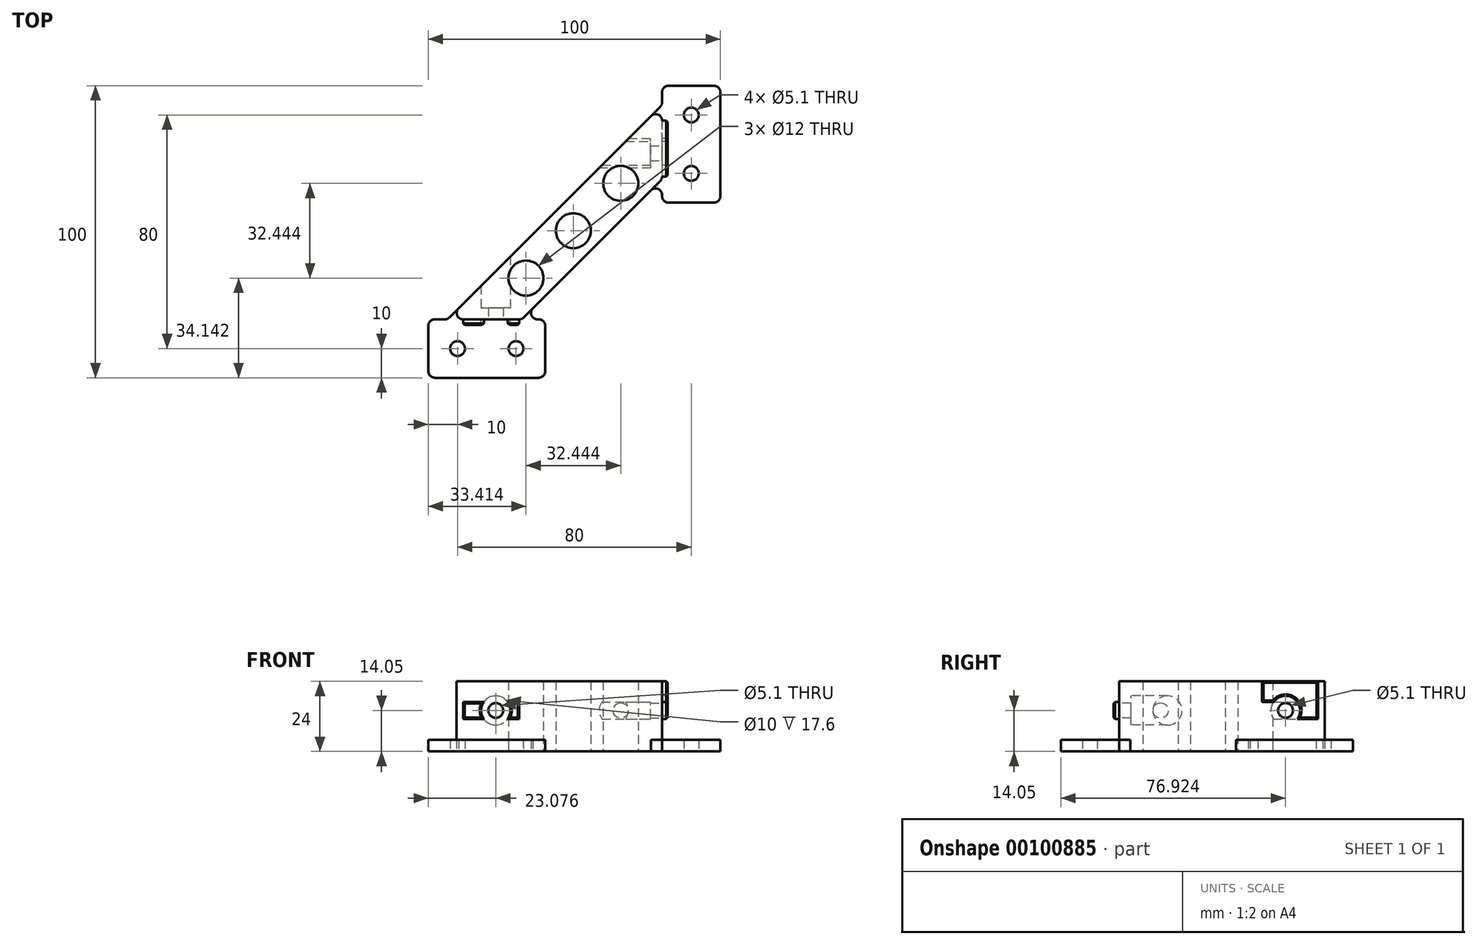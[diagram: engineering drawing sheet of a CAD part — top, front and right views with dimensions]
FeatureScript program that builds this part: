
annotation { "Feature Type Name" : "Feature", "Feature Type Description" : "" }
export const myFeature = defineFeature(function(context is Context, id is Id, definition is map)
    precondition{}
    {
        {
            var Q0;
            Q0=qCreatedBy(makeId("Top.planeOp"),FACE);
            var sketch = newSketch(context, id + "F0", { "sketchPlane" : qUnion([Q0])});
            skLineSegment(sketch, "E0.bottom", {"start": v(2.23, 0) * mm, "end": v(37.77, 0) * mm});
            skLineSegment(sketch, "E0.top", {"start": v(37.39, 20) * mm, "end": v(37.77, 20) * mm});
            skLineSegment(sketch, "E0.left", {"start": v(0, 2.23) * mm, "end": v(0, 17.77) * mm});
            skLineSegment(sketch, "E0.right", {"start": v(40, 2.23) * mm, "end": v(40, 17.77) * mm});
            skLineSegment(sketch, "E1", {"start": v(0, 0) * mm, "end": v(100, 0) * mm, "construction": true});
            skLineSegment(sketch, "E2", {"start": v(100, 0) * mm, "end": v(100, 100) * mm, "construction": true});
            skLineSegment(sketch, "E3.bottom", {"start": v(97.77, 100) * mm, "end": v(82.23, 100) * mm});
            skLineSegment(sketch, "E3.top", {"start": v(97.77, 60) * mm, "end": v(82.23, 60) * mm});
            skLineSegment(sketch, "E3.left", {"start": v(100, 97.77) * mm, "end": v(100, 62.23) * mm});
            skLineSegment(sketch, "E3.right", {"start": v(80, 62.61) * mm, "end": v(80, 62.23) * mm});
            skLineSegment(sketch, "E4", {"start": v(40, 20) * mm, "end": v(32, 20) * mm, "construction": true});
            skLineSegment(sketch, "E5", {"start": v(2.23, 20) * mm, "end": v(5.62, 20) * mm});
            skLineSegment(sketch, "E6", {"start": v(80, 60) * mm, "end": v(80, 68) * mm, "construction": true});
            skLineSegment(sketch, "E7", {"start": v(80, 97.77) * mm, "end": v(80, 94.38) * mm});
            skLineSegment(sketch, "E8", {"start": v(76.2, 64.2) * mm, "end": v(35.8, 23.8) * mm});
            skLineSegment(sketch, "E9", {"start": v(76.2, 89.65) * mm, "end": v(10.35, 23.8) * mm});
            skLineSegment(sketch, "E10", {"start": v(90, 80) * mm, "end": v(90, 70) * mm, "construction": true});
            skLineSegment(sketch, "E11", {"start": v(90, 80) * mm, "end": v(90, 90) * mm, "construction": true});
            skCircle(sketch, "E12", {"center": v(90, 90) * mm, "radius": 2.55 * mm});
            skCircle(sketch, "E13", {"center": v(90, 70) * mm, "radius": 2.55 * mm});
            skLineSegment(sketch, "E14", {"start": v(20, 10) * mm, "end": v(10, 10) * mm, "construction": true});
            skPoint(sketch, "E14.endSnap0", {"position": v(0, 10) * mm});
            skLineSegment(sketch, "E15", {"start": v(20, 10) * mm, "end": v(30, 10) * mm, "construction": true});
            skCircle(sketch, "E16", {"center": v(30, 10) * mm, "radius": 2.55 * mm});
            skCircle(sketch, "E17", {"center": v(10, 10) * mm, "radius": 2.55 * mm});
            skPoint(sketch, "E18.newPointA", {"position": v(32, 20) * mm});
            skArc(sketch, "E18.filletArc", {"start": v(35.8, 23.8) * mm, "mid": v(35.33, 21.38) * mm, "end": v(37.39, 20) * mm});
            skPoint(sketch, "E19.visualSharp", {"position": v(6.54, 20) * mm});
            skArc(sketch, "E19.filletArc", {"start": v(5.62, 20) * mm, "mid": v(6.47, 20.17) * mm, "end": v(7.2, 20.65) * mm});
            skArc(sketch, "E20.filletArc", {"start": v(80, 62.61) * mm, "mid": v(78.62, 64.67) * mm, "end": v(76.2, 64.2) * mm});
            skPoint(sketch, "E21.visualSharp", {"position": v(80, 93.46) * mm});
            skArc(sketch, "E21.filletArc", {"start": v(79.35, 92.8) * mm, "mid": v(79.83, 93.53) * mm, "end": v(80, 94.38) * mm});
            skLineSegment(sketch, "E22", {"start": v(80, 88.07) * mm, "end": v(80, 68.92) * mm});
            skLineSegment(sketch, "E23", {"start": v(11.93, 20) * mm, "end": v(31.08, 20) * mm});
            skCircle(sketch, "E24", {"center": v(33.41, 34.14) * mm, "radius": 6 * mm});
            skCircle(sketch, "E25", {"center": v(65.86, 66.59) * mm, "radius": 6 * mm});
            skCircle(sketch, "E26", {"center": v(49.64, 50.36) * mm, "radius": 6 * mm});
            skPoint(sketch, "E27.visualSharp", {"position": v(0, 20) * mm});
            skArc(sketch, "E27.filletArc", {"start": v(2.23, 20) * mm, "mid": v(0.65, 19.35) * mm, "end": v(0, 17.77) * mm});
            skPoint(sketch, "E28.visualSharp", {"position": v(0, 0) * mm});
            skArc(sketch, "E28.filletArc", {"start": v(0, 2.23) * mm, "mid": v(0.65, 0.65) * mm, "end": v(2.23, 0) * mm});
            skPoint(sketch, "E29.visualSharp", {"position": v(40, 0) * mm});
            skArc(sketch, "E29.filletArc", {"start": v(37.77, 0) * mm, "mid": v(39.35, 0.65) * mm, "end": v(40, 2.23) * mm});
            skPoint(sketch, "E30.visualSharp", {"position": v(40, 20) * mm});
            skArc(sketch, "E30.filletArc", {"start": v(40, 17.77) * mm, "mid": v(39.35, 19.35) * mm, "end": v(37.77, 20) * mm});
            skPoint(sketch, "E31.visualSharp", {"position": v(100, 60) * mm});
            skArc(sketch, "E31.filletArc", {"start": v(97.77, 60) * mm, "mid": v(99.35, 60.65) * mm, "end": v(100, 62.23) * mm});
            skPoint(sketch, "E32.visualSharp", {"position": v(80, 60) * mm});
            skArc(sketch, "E32.filletArc", {"start": v(80, 62.23) * mm, "mid": v(80.65, 60.65) * mm, "end": v(82.23, 60) * mm});
            skPoint(sketch, "E33.visualSharp", {"position": v(80, 100) * mm});
            skArc(sketch, "E33.filletArc", {"start": v(82.23, 100) * mm, "mid": v(80.65, 99.35) * mm, "end": v(80, 97.77) * mm});
            skPoint(sketch, "E34.visualSharp", {"position": v(100, 100) * mm});
            skArc(sketch, "E34.filletArc", {"start": v(100, 97.77) * mm, "mid": v(99.35, 99.35) * mm, "end": v(97.77, 100) * mm});
            skArc(sketch, "E35.filletArc", {"start": v(80, 88.07) * mm, "mid": v(78.62, 90.13) * mm, "end": v(76.2, 89.65) * mm});
            skLineSegment(sketch, "E36", {"start": v(79.35, 92.8) * mm, "end": v(76.2, 89.65) * mm});
            skLineSegment(sketch, "E37", {"start": v(76.2, 64.2) * mm, "end": v(79.35, 67.35) * mm});
            skArc(sketch, "E38.filletArc", {"start": v(79.35, 67.35) * mm, "mid": v(79.83, 68.07) * mm, "end": v(80, 68.92) * mm});
            skLineSegment(sketch, "E39", {"start": v(35.8, 23.8) * mm, "end": v(32.65, 20.65) * mm});
            skArc(sketch, "E40.filletArc", {"start": v(31.08, 20) * mm, "mid": v(31.93, 20.17) * mm, "end": v(32.65, 20.65) * mm});
            skArc(sketch, "E41.filletArc", {"start": v(10.35, 23.8) * mm, "mid": v(9.87, 21.38) * mm, "end": v(11.93, 20) * mm});
            skLineSegment(sketch, "E42", {"start": v(7.2, 20.65) * mm, "end": v(10.35, 23.8) * mm});
            skSolve(sketch);
        }
        {
            var Q0;
            Q0=makeQuery(id+"F0.imprint","IMPRINT",FACE,{"disambiguationData":[TD([[makeQuery(id+"F0.imprint","IMPRINT",EDGE,{"derivedFrom":sQuery(id+"F0.wireOp",EDGE,"E0.bottom")}),1.0]])]});
            var Q1;
            Q1=makeQuery(id+"F0.imprint","IMPRINT",FACE,{"disambiguationData":[TD([[makeQuery(id+"F0.imprint","IMPRINT",EDGE,{"derivedFrom":sQuery(id+"F0.wireOp",EDGE,"E3.bottom")}),1.0]])]});
            extrude(context, id + "F1", {"entities" : qUnion([Q0, Q1]), "depth" : 4 * mm});
        }
        {
            var Q0;
            Q0=makeQuery(id+"F0.imprint","IMPRINT",FACE,{"disambiguationData":[TD([[makeQuery(id+"F0.imprint","IMPRINT",EDGE,{"derivedFrom":sQuery(id+"F0.wireOp",EDGE,"E8")}),-1.0]])]});
            extrude(context, id + "F2", {"entities" : qUnion([Q0]), "depth" : 24 * mm});
        }
        {
            var Q0;
            Q0=makeQuery(id+"F2.opExtrude","SWEPT_FACE",FACE,{"disambiguationData":[OSD([sQuery(id+"F0.wireOp",EDGE,"E22")])]});
            var sketch = newSketch(context, id + "F3", { "sketchPlane" : qUnion([Q0])});
            skCircle(sketch, "E43", {"center": v(76.92, 14.05) * mm, "radius": 2.55 * mm});
            skCircle(sketch, "E44", {"center": v(76.92, 14.05) * mm, "radius": 5 * mm});
            skLineSegment(sketch, "E45", {"start": v(68.92, 11.15) * mm, "end": v(88.07, 11.15) * mm});
            skLineSegment(sketch, "E46", {"start": v(76.92, 16.95) * mm, "end": v(68.92, 16.95) * mm});
            skLineSegment(sketch, "E47", {"start": v(68.92, 16.95) * mm, "end": v(88.07, 16.95) * mm});
            skLineSegment(sketch, "E48", {"start": v(76.92, 14.05) * mm, "end": v(68.92, 14.05) * mm, "construction": true});
            skLineSegment(sketch, "E49", {"start": v(70.24, 14.05) * mm, "end": v(70.24, 16.95) * mm, "construction": true});
            skLineSegment(sketch, "E50", {"start": v(70.24, 14.05) * mm, "end": v(70.24, 11.15) * mm, "construction": true});
            skLineSegment(sketch, "E51.bottom", {"start": v(79.82, 11.15) * mm, "end": v(74.02, 11.15) * mm});
            skLineSegment(sketch, "E51.top", {"start": v(79.82, 16.95) * mm, "end": v(74.02, 16.95) * mm});
            skLineSegment(sketch, "E51.left", {"start": v(79.82, 11.15) * mm, "end": v(79.82, 16.95) * mm});
            skLineSegment(sketch, "E51.right", {"start": v(74.02, 11.15) * mm, "end": v(74.02, 16.95) * mm});
            skSolve(sketch);
        }
        {
            var Q0;
            Q0=makeQuery(id+"F3.imprint","IMPRINT",FACE,{"disambiguationData":[TD([[makeQuery(id+"F3.imprint","IMPRINT",EDGE,{"derivedFrom":sQuery(id+"F3.wireOp",EDGE,"E43")}),1.0]])]});
            extrude(context, id + "F4", {"entities" : qUnion([Q0]), "operationType" : NewBodyOperationType.REMOVE, "oppositeDirection" : true, "depth" : 25 * mm});
        }
        {
            var Q0;
            Q0=makeQuery(id+"F3.imprint","IMPRINT",FACE,{"disambiguationData":[TD([[makeQuery(id+"F3.imprint","IMPRINT",EDGE,{"derivedFrom":sQuery(id+"F3.wireOp",EDGE,"E43")}),-1.0]])]});
            var Q1;
            {var subQ0=sQuery(id+"F3.wireOp",EDGE,"E47");var subQ4=makeQuery(id+"F3.imprint","IMPRINT",VERTEX,{"derivedFrom":subQ0});Q1=makeQuery(id+"F3.imprint","IMPRINT",FACE,{"disambiguationData":[TD([[makeQuery(id+"F3.imprint","IMPRINT",EDGE,{"disambiguationData":[TD([[subQ4,1.0]])],"derivedFrom":subQ0}),1.0]])]});}
            var Q2;
            {var subQ0=sQuery(id+"F3.wireOp",EDGE,"E45");var subQ1=sQuery(id+"F3.wireOp",EDGE,"E44");var subQ2=makeQuery(id+"F3.imprint","INTERSECT",VERTEX,{"disambiguationData":[OD(0.0)],"derivedFrom":[subQ1,subQ0]});Q2=makeQuery(id+"F3.imprint","IMPRINT",FACE,{"disambiguationData":[TD([[makeQuery(id+"F3.imprint","IMPRINT",EDGE,{"disambiguationData":[TD([[subQ2,-1.0]])],"derivedFrom":subQ1}),1.0]])]});}
            var Q3;
            Q3=makeQuery(id+"F2.opExtrude","SWEPT_FACE",FACE,{"disambiguationData":[OSD([sQuery(id+"F0.wireOp",EDGE,"E9")])]});
            var Q4;
            {var subQ1=sQuery(id+"F3.wireOp",EDGE,"E47");var subQ4=sQuery(id+"F3.wireOp",EDGE,"E44");var subQ6=makeQuery(id+"F3.imprint","INTERSECT",VERTEX,{"disambiguationData":[OD(0.0)],"derivedFrom":[subQ4,subQ1]});Q4=makeQuery(id+"F3.imprint","IMPRINT",FACE,{"disambiguationData":[TD([[makeQuery(id+"F3.imprint","IMPRINT",EDGE,{"disambiguationData":[TD([[subQ6,1.0]])],"derivedFrom":subQ4}),1.0]])]});}
            var Q5;
            {var subQ5=sQuery(id+"F3.wireOp",EDGE,"E51.left");Q5=makeQuery(id+"F3.imprint","IMPRINT",FACE,{"disambiguationData":[TD([[makeQuery(id+"F3.imprint","IMPRINT",EDGE,{"derivedFrom":subQ5}),-1.0]])]});}
            var Q6;
            {var subQ5=sQuery(id+"F3.wireOp",EDGE,"E51.right");Q6=makeQuery(id+"F3.imprint","IMPRINT",FACE,{"disambiguationData":[TD([[makeQuery(id+"F3.imprint","IMPRINT",EDGE,{"derivedFrom":subQ5}),1.0]])]});}
            extrude(context, id + "F5", {"entities" : qUnion([Q0, Q1, Q2, Q3, Q4, Q5, Q6]), "operationType" : NewBodyOperationType.REMOVE, "oppositeDirection" : true, "depth" : 51.78 * mm, "hasSecondDirection" : true, "secondDirectionOppositeDirection" : true, "secondDirectionDepth" : 4 * mm});
        }
        {
            var Q0;
            {var subQ0=sQuery(id+"F3.wireOp",EDGE,"E47");var subQ1=sQuery(id+"F3.wireOp",EDGE,"E44");var subQ2=makeQuery(id+"F3.imprint","INTERSECT",VERTEX,{"disambiguationData":[OD(0.0)],"derivedFrom":[subQ1,subQ0]});Q0=makeQuery(id+"F3.imprint","IMPRINT",FACE,{"disambiguationData":[TD([[makeQuery(id+"F3.imprint","IMPRINT",EDGE,{"disambiguationData":[TD([[subQ2,-1.0]])],"derivedFrom":subQ1}),-1.0]])]});}
            var Q1;
            {var subQ0=sQuery(id+"F3.wireOp",EDGE,"E47");var subQ1=sQuery(id+"F3.wireOp",EDGE,"E44");var subQ2=makeQuery(id+"F3.imprint","INTERSECT",VERTEX,{"disambiguationData":[OD(1.0)],"derivedFrom":[subQ1,subQ0]});Q1=makeQuery(id+"F3.imprint","IMPRINT",FACE,{"disambiguationData":[TD([[makeQuery(id+"F3.imprint","IMPRINT",EDGE,{"disambiguationData":[TD([[subQ2,1.0]])],"derivedFrom":subQ1}),-1.0]])]});}
            extrude(context, id + "F6", {"entities" : qUnion([Q0, Q1]), "operationType" : NewBodyOperationType.ADD, "depth" : 1.9 * mm});
        }
        {
            var Q0;
            Q0=makeQuery(id+"F2.opExtrude","SWEPT_FACE",FACE,{"disambiguationData":[OSD([sQuery(id+"F0.wireOp",EDGE,"E23")])]});
            var sketch = newSketch(context, id + "F7", { "sketchPlane" : qUnion([Q0])});
            skLineSegment(sketch, "E52", {"start": v(23.08, 14.05) * mm, "end": v(31.08, 14.05) * mm, "construction": true});
            skCircle(sketch, "E53", {"center": v(23.08, 14.05) * mm, "radius": 2.55 * mm});
            skCircle(sketch, "E54", {"center": v(23.08, 14.05) * mm, "radius": 5 * mm});
            skLineSegment(sketch, "E55", {"start": v(31.08, 16.95) * mm, "end": v(11.93, 16.95) * mm});
            skLineSegment(sketch, "E56", {"start": v(31.08, 11.15) * mm, "end": v(11.93, 11.15) * mm});
            skLineSegment(sketch, "E57", {"start": v(28.9, 14.05) * mm, "end": v(28.9, 16.95) * mm, "construction": true});
            skLineSegment(sketch, "E58", {"start": v(29.62, 14.05) * mm, "end": v(29.62, 11.15) * mm, "construction": true});
            skLineSegment(sketch, "E59.bottom", {"start": v(25.98, 11.15) * mm, "end": v(20.18, 11.15) * mm});
            skLineSegment(sketch, "E59.top", {"start": v(25.98, 16.95) * mm, "end": v(20.18, 16.95) * mm});
            skLineSegment(sketch, "E59.left", {"start": v(25.98, 11.15) * mm, "end": v(25.98, 16.95) * mm});
            skLineSegment(sketch, "E59.right", {"start": v(20.18, 11.15) * mm, "end": v(20.18, 16.95) * mm});
            skSolve(sketch);
        }
        {
            var Q0;
            Q0=makeQuery(id+"F7.imprint","IMPRINT",FACE,{"disambiguationData":[TD([[makeQuery(id+"F7.imprint","IMPRINT",EDGE,{"derivedFrom":sQuery(id+"F7.wireOp",EDGE,"E53")}),1.0]])]});
            extrude(context, id + "F8", {"entities" : qUnion([Q0]), "operationType" : NewBodyOperationType.REMOVE, "oppositeDirection" : true, "depth" : 22.92 * mm});
        }
        {
            var Q0;
            Q0=makeQuery(id+"F7.imprint","IMPRINT",FACE,{"disambiguationData":[TD([[makeQuery(id+"F7.imprint","IMPRINT",EDGE,{"derivedFrom":sQuery(id+"F7.wireOp",EDGE,"E53")}),-1.0]])]});
            var Q1;
            {var subQ0=sQuery(id+"F7.wireOp",EDGE,"E55");var subQ1=sQuery(id+"F7.wireOp",EDGE,"E54");var subQ2=makeQuery(id+"F7.imprint","INTERSECT",VERTEX,{"disambiguationData":[OD(0.0)],"derivedFrom":[subQ1,subQ0]});Q1=makeQuery(id+"F7.imprint","IMPRINT",FACE,{"disambiguationData":[TD([[makeQuery(id+"F7.imprint","IMPRINT",EDGE,{"disambiguationData":[TD([[subQ2,1.0]])],"derivedFrom":subQ1}),1.0]])]});}
            var Q2;
            {var subQ0=sQuery(id+"F7.wireOp",EDGE,"E56");var subQ1=sQuery(id+"F7.wireOp",EDGE,"E54");var subQ2=makeQuery(id+"F7.imprint","INTERSECT",VERTEX,{"disambiguationData":[OD(0.0)],"derivedFrom":[subQ1,subQ0]});Q2=makeQuery(id+"F7.imprint","IMPRINT",FACE,{"disambiguationData":[TD([[makeQuery(id+"F7.imprint","IMPRINT",EDGE,{"disambiguationData":[TD([[subQ2,-1.0]])],"derivedFrom":subQ1}),1.0]])]});}
            var Q3;
            {var subQ5=sQuery(id+"F7.wireOp",EDGE,"E59.right");Q3=makeQuery(id+"F7.imprint","IMPRINT",FACE,{"disambiguationData":[TD([[makeQuery(id+"F7.imprint","IMPRINT",EDGE,{"derivedFrom":subQ5}),1.0]])]});}
            var Q4;
            {var subQ5=sQuery(id+"F7.wireOp",EDGE,"E59.left");Q4=makeQuery(id+"F7.imprint","IMPRINT",FACE,{"disambiguationData":[TD([[makeQuery(id+"F7.imprint","IMPRINT",EDGE,{"derivedFrom":subQ5}),-1.0]])]});}
            extrude(context, id + "F9", {"entities" : qUnion([Q0, Q1, Q2, Q3, Q4]), "operationType" : NewBodyOperationType.REMOVE, "oppositeDirection" : true, "depth" : 25 * mm, "hasSecondDirection" : true, "secondDirectionOppositeDirection" : true, "secondDirectionDepth" : 4 * mm});
        }
        {
            var Q0;
            {var subQ0=sQuery(id+"F7.wireOp",EDGE,"E55");var subQ1=sQuery(id+"F7.wireOp",EDGE,"E54");var subQ2=makeQuery(id+"F7.imprint","INTERSECT",VERTEX,{"disambiguationData":[OD(0.0)],"derivedFrom":[subQ1,subQ0]});Q0=makeQuery(id+"F7.imprint","IMPRINT",FACE,{"disambiguationData":[TD([[makeQuery(id+"F7.imprint","IMPRINT",EDGE,{"disambiguationData":[TD([[subQ2,-1.0]])],"derivedFrom":subQ1}),-1.0]])]});}
            var Q1;
            {var subQ0=sQuery(id+"F7.wireOp",EDGE,"E55");var subQ1=sQuery(id+"F7.wireOp",EDGE,"E54");var subQ2=makeQuery(id+"F7.imprint","INTERSECT",VERTEX,{"disambiguationData":[OD(1.0)],"derivedFrom":[subQ1,subQ0]});Q1=makeQuery(id+"F7.imprint","IMPRINT",FACE,{"disambiguationData":[TD([[makeQuery(id+"F7.imprint","IMPRINT",EDGE,{"disambiguationData":[TD([[subQ2,1.0]])],"derivedFrom":subQ1}),-1.0]])]});}
            extrude(context, id + "F10", {"entities" : qUnion([Q0, Q1]), "operationType" : NewBodyOperationType.ADD, "depth" : 1.9 * mm});
        }
        {
            var Q0;
            Q0=makeQuery(id+"F6.opExtrude","CAP_FACE",FACE,{"disambiguationData":[OSD([sQuery(id+"F0.wireOp",EDGE,"E22"),sQuery(id+"F0.wireOp",EDGE,"E35.filletArc"),sQuery(id+"F3.wireOp",EDGE,"E44"),sQuery(id+"F3.wireOp",EDGE,"E45"),sQuery(id+"F3.wireOp",EDGE,"E47")])],"isStart":false});
            var Q1;
            Q1=makeQuery(id+"F6.opExtrude","CAP_FACE",FACE,{"disambiguationData":[OSD([sQuery(id+"F0.wireOp",EDGE,"E22"),sQuery(id+"F0.wireOp",EDGE,"E38.filletArc"),sQuery(id+"F3.wireOp",EDGE,"E44"),sQuery(id+"F3.wireOp",EDGE,"E45"),sQuery(id+"F3.wireOp",EDGE,"E47")])],"isStart":false});
            var Q2;
            Q2=makeQuery(id+"F10.opExtrude","CAP_FACE",FACE,{"disambiguationData":[OSD([sQuery(id+"F0.wireOp",EDGE,"E23"),sQuery(id+"F0.wireOp",EDGE,"E40.filletArc"),sQuery(id+"F7.wireOp",EDGE,"E54"),sQuery(id+"F7.wireOp",EDGE,"E55"),sQuery(id+"F7.wireOp",EDGE,"E56")])],"isStart":false});
            var Q3;
            Q3=makeQuery(id+"F10.opExtrude","CAP_FACE",FACE,{"disambiguationData":[OSD([sQuery(id+"F0.wireOp",EDGE,"E23"),sQuery(id+"F0.wireOp",EDGE,"E41.filletArc"),sQuery(id+"F7.wireOp",EDGE,"E54"),sQuery(id+"F7.wireOp",EDGE,"E55"),sQuery(id+"F7.wireOp",EDGE,"E56")])],"isStart":false});
            chamfer(context, id + "F11", {"entities" : qUnion([Q0, Q1, Q2, Q3]), "width" : .5 * mm, "tangentPropagation" : true});
        }
    });
